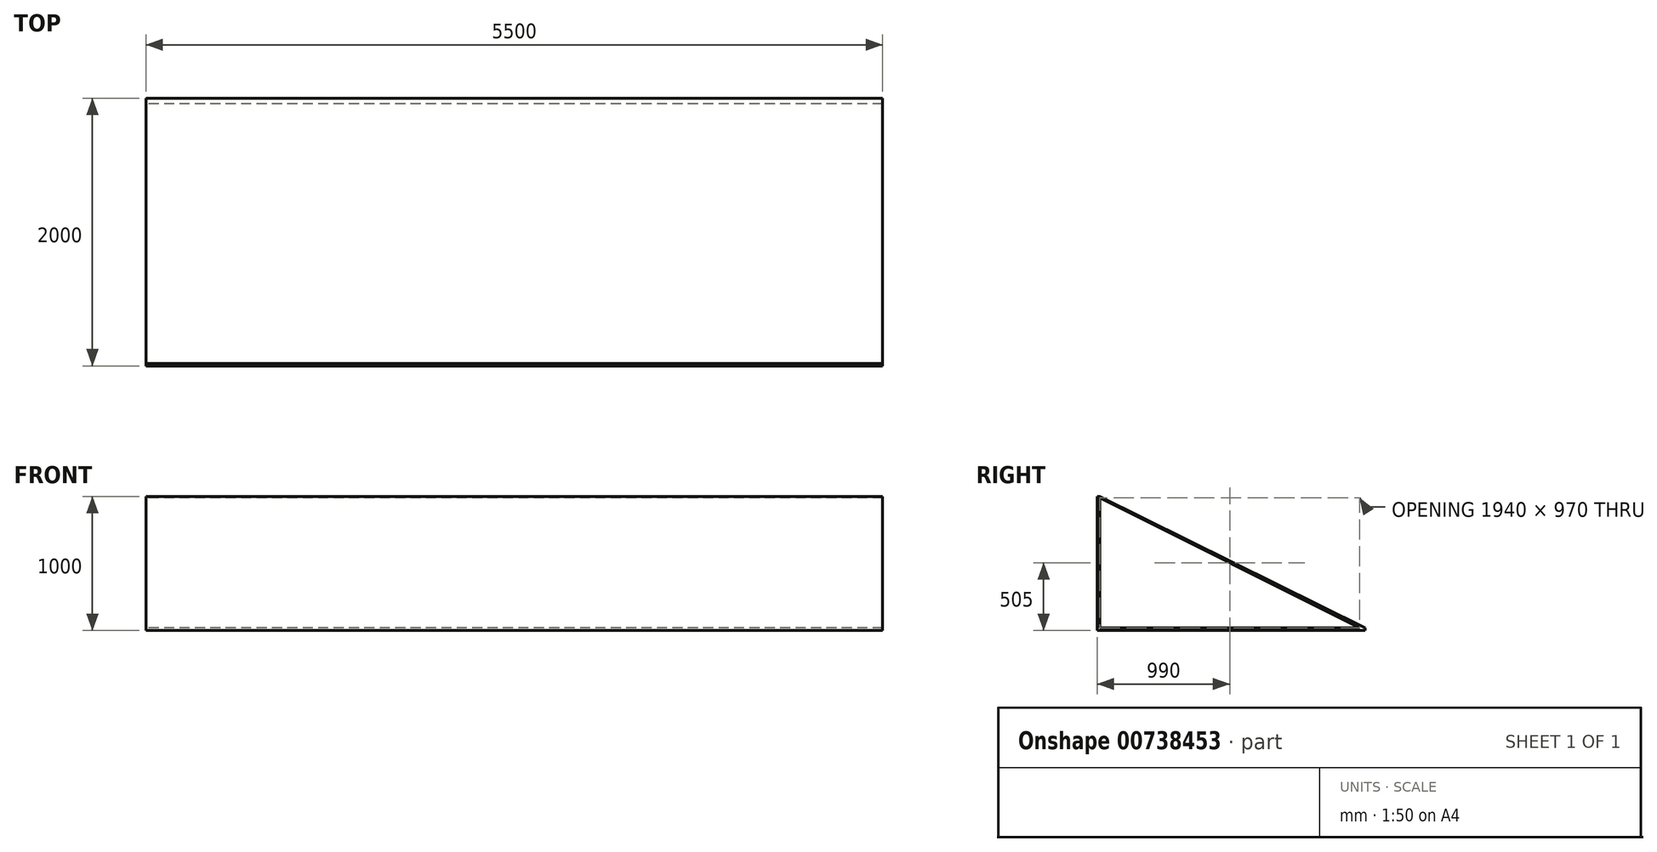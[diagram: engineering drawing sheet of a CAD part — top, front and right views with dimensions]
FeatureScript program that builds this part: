
annotation { "Feature Type Name" : "Feature", "Feature Type Description" : "" }
export const myFeature = defineFeature(function(context is Context, id is Id, definition is map)
    precondition{}
    {
        {
            var Q0;
            Q0=qCreatedBy(makeId("Right.planeOp"),FACE);
            var sketch = newSketch(context, id + "F0", { "sketchPlane" : qUnion([Q0])});
            skLineSegment(sketch, "E0.bottom", {"start": v(0, 0) * mm, "end": v(20, 0) * mm});
            skLineSegment(sketch, "E0.top", {"start": v(0, 1000) * mm, "end": v(20, 1000) * mm});
            skLineSegment(sketch, "E0.left", {"start": v(0, 0) * mm, "end": v(0, 1000) * mm});
            skLineSegment(sketch, "E0.right", {"start": v(20, 20) * mm, "end": v(20, 990) * mm});
            skLineSegment(sketch, "E1.bottom", {"start": v(0, 0) * mm, "end": v(2000, 0) * mm});
            skLineSegment(sketch, "E1.top", {"start": v(20, 20) * mm, "end": v(1960, 20) * mm});
            skLineSegment(sketch, "E1.left", {"start": v(0, 0) * mm, "end": v(0, 20) * mm});
            skLineSegment(sketch, "E1.right", {"start": v(2000, 0) * mm, "end": v(2000, 20) * mm});
            skLineSegment(sketch, "E2", {"start": v(20, 1000) * mm, "end": v(2000, 20) * mm});
            skLineSegment(sketch, "E3", {"start": v(20, 990) * mm, "end": v(1960, 20) * mm});
            skSolve(sketch);
        }
        {
            var Q0;
            Q0=qSketchRegion(id+"F0",true);
            extrude(context, id + "F1", {"entities" : qUnion([Q0]), "depth" : 5500 * mm, "offsetDistance" : 25 * mm});
        }
    });
